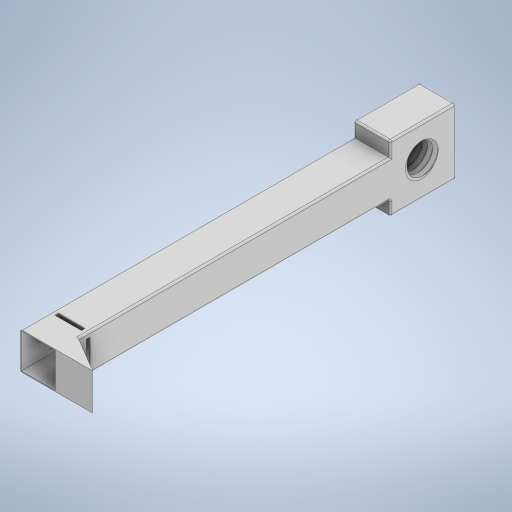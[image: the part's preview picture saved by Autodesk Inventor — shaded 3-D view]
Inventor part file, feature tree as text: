
AUTODESK INVENTOR PART (.ipt)
format: ipt  version: 2024 (Build 280153000, 153)  size: 511,488 bytes
history: native  units: mm
features: sketch x10, extrude x9, other x1, fillet x1
ambient origin geometry x8: Origin, YZ Plane, XZ Plane, XY Plane, X Axis, Y Axis, Z Axis, Center Point
bodies: Volumenkörper1 (feature_tree)
feature tree (21):
  extrude  "Extrusion1"  Depth=10.0mm
  extrude  "Extrusion2"  Depth=10.0mm
  extrude  "Extrusion3"  Depth=18.0mm TaperAngle=0.0deg
  extrude  "Extrusion4"  Depth=9.0mm TaperAngle=0.0deg
  other  "Spirale1"
  extrude  "Extrusion6"  Depth=9.0mm TaperAngle=0.0deg
  extrude  "Extrusion7"  Depth=10.0mm
  extrude  "Extrusion8"  Depth=0.2mm
  extrude  "Extrusion9"  Depth=9.5mm
  fillet  "Rundung2"  Radius=9.5mm
  extrude  "Extrusion10"  Depth=1.1mm
  sketch  "Skizze1"  dims[d0=10.0mm d1=10.0mm]
  sketch  "Skizze2"  dims[d2=91.0mm d3=0.0mm d4=10.0mm]
  sketch  "Skizze3"  dims[d5=18.0mm d6=18.0mm d7=0.0mm]
  sketch  "Skizze4"  dims[d8=10.0mm d9=9.0mm d10=0.0mm]
  sketch  "Skizze5"  dims[d17=7.2mm d18=9.0mm d19=0.0mm]
  sketch  "Skizze7"  dims[d22=1.4mm d23=11.0mm d24=10.0mm d25=0.0mm d26=90.0deg d27=90.0deg d28=0.0mm d29=0.0mm d33=1.7mm]
  sketch  "Skizze8"  dims[d34=60.0deg d35=0.2mm]
  sketch  "Skizze9"  dims[d36=1.0mm d37=0.0mm d39=9.5mm d40=9.5mm]
  sketch  "Skizze10"  dims[d41=9.0mm d42=0.0mm d43=1.1mm]
  sketch  "Skizze11"  dims[d44=1.1mm d45=0.5mm d46=0.5mm d47=1.1mm d48=1.1mm d49=1.1mm d50=1.1mm d51=0.5mm d52=0.5mm d53=1.0mm d54=0.0mm d55=2.0mm d56=0.0mm d57=0.5mm d59=0.5mm d60=10.0mm d61=0.0mm d38=0.0mm]
